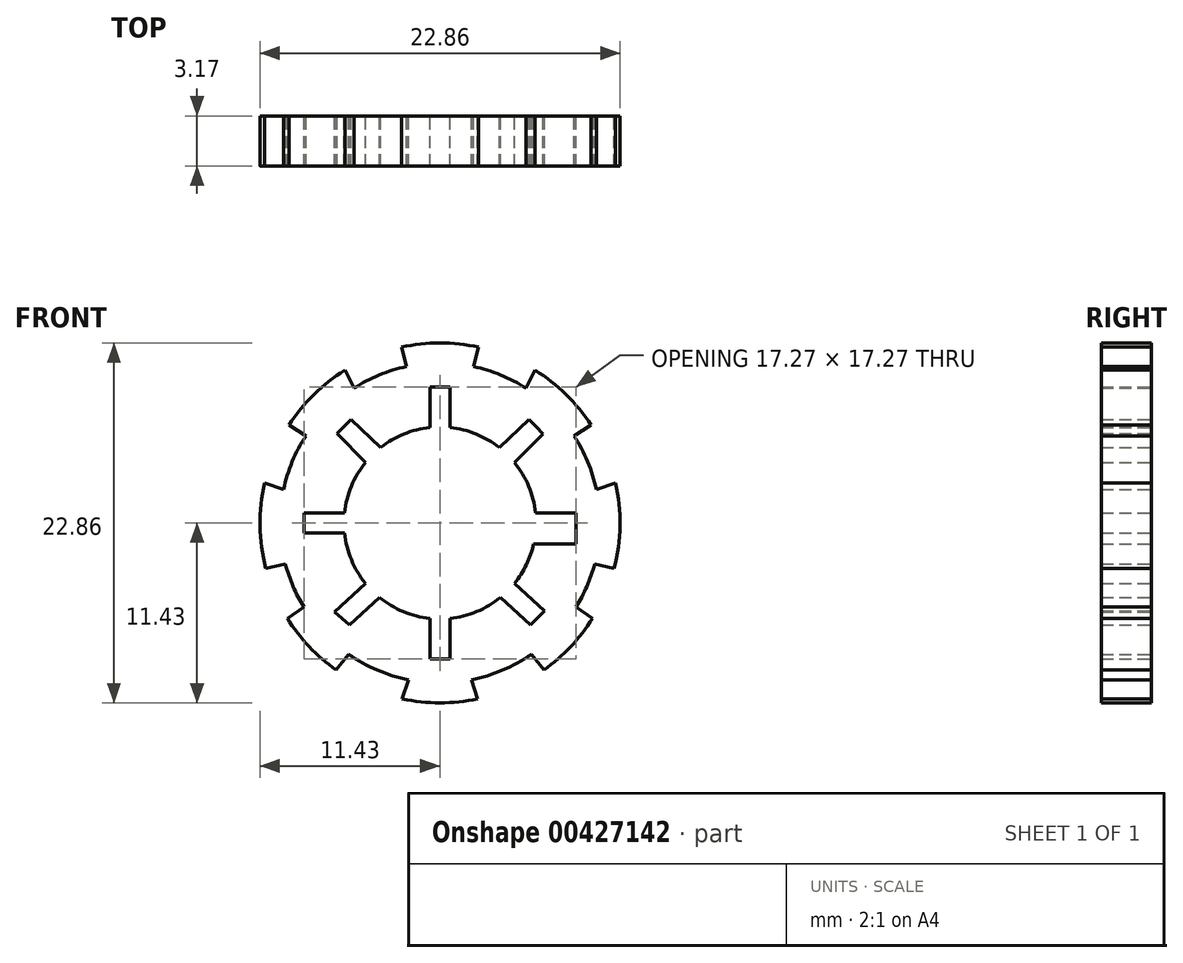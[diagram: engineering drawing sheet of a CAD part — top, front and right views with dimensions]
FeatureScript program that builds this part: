
annotation { "Feature Type Name" : "Feature", "Feature Type Description" : "" }
export const myFeature = defineFeature(function(context is Context, id is Id, definition is map)
    precondition{}
    {
        {
            var Q0;
            Q0=qCreatedBy(makeId("Front.planeOp"),FACE);
            var sketch = newSketch(context, id + "F0", { "sketchPlane" : qUnion([Q0])});
            skCircle(sketch, "E0", {"center": v(0, 0) * mm, "radius": 12.7 * mm});
            skCircle(sketch, "E1", {"center": v(0, 0) * mm, "radius": 11.43 * mm});
            skCircle(sketch, "E2", {"center": v(0, 0) * mm, "radius": 10.16 * mm});
            skCircle(sketch, "E3", {"center": v(0, 0) * mm, "radius": 6.1 * mm});
            skLineSegment(sketch, "E4", {"start": v(0, 8.64) * mm, "end": v(-0.63, 8.64) * mm});
            skLineSegment(sketch, "E5", {"start": v(0, 8.64) * mm, "end": v(0.64, 8.64) * mm});
            skLineSegment(sketch, "E6", {"start": v(6.1, 6.1) * mm, "end": v(5.66, 6.56) * mm});
            skLineSegment(sketch, "E7", {"start": v(6.1, 6.1) * mm, "end": v(6.56, 5.66) * mm});
            skLineSegment(sketch, "E8", {"start": v(8.64, 0) * mm, "end": v(8.64, 0.63) * mm});
            skLineSegment(sketch, "E9", {"start": v(8.64, 0) * mm, "end": v(8.64, -0.64) * mm});
            skLineSegment(sketch, "E10", {"start": v(0, -8.64) * mm, "end": v(-0.63, -8.64) * mm});
            skLineSegment(sketch, "E11", {"start": v(0, -8.64) * mm, "end": v(0.64, -8.64) * mm});
            skLineSegment(sketch, "E12", {"start": v(-8.64, 0) * mm, "end": v(-8.64, 0.63) * mm});
            skLineSegment(sketch, "E13", {"start": v(-8.64, 0) * mm, "end": v(-8.64, -0.64) * mm});
            skLineSegment(sketch, "E14", {"start": v(-6.1, 6.12) * mm, "end": v(-6.54, 5.67) * mm});
            skLineSegment(sketch, "E15", {"start": v(-6.1, 6.12) * mm, "end": v(-5.66, 6.58) * mm});
            skLineSegment(sketch, "E16", {"start": v(-8.64, 0.63) * mm, "end": v(-6.06, 0.63) * mm});
            skLineSegment(sketch, "E17", {"start": v(-8.64, -0.64) * mm, "end": v(-6.06, -0.64) * mm});
            skLineSegment(sketch, "E18", {"start": v(-6.54, 5.67) * mm, "end": v(-4.72, 3.85) * mm});
            skLineSegment(sketch, "E19", {"start": v(-5.66, 6.58) * mm, "end": v(-3.77, 4.8) * mm});
            skLineSegment(sketch, "E20", {"start": v(-0.63, 8.64) * mm, "end": v(-0.63, 6.06) * mm});
            skLineSegment(sketch, "E21", {"start": v(0.64, 8.64) * mm, "end": v(0.64, 6.06) * mm});
            skLineSegment(sketch, "E22", {"start": v(5.66, 6.56) * mm, "end": v(3.84, 4.74) * mm});
            skLineSegment(sketch, "E23", {"start": v(6.56, 5.66) * mm, "end": v(4.74, 3.84) * mm});
            skLineSegment(sketch, "E24", {"start": v(8.64, 0.63) * mm, "end": v(6.06, 0.63) * mm});
            skLineSegment(sketch, "E25", {"start": v(8.64, -0.64) * mm, "end": v(6.06, -0.64) * mm});
            skLineSegment(sketch, "E26", {"start": v(-6.68, -5.64) * mm, "end": v(-4.74, -3.84) * mm});
            skLineSegment(sketch, "E27", {"start": v(-5.73, -6.48) * mm, "end": v(-3.84, -4.73) * mm});
            skLineSegment(sketch, "E28", {"start": v(-0.63, -8.64) * mm, "end": v(-0.63, -6.06) * mm});
            skLineSegment(sketch, "E29", {"start": v(0.64, -8.64) * mm, "end": v(0.64, -6.06) * mm});
            skLineSegment(sketch, "E30", {"start": v(6.63, -5.59) * mm, "end": v(4.74, -3.84) * mm});
            skLineSegment(sketch, "E31", {"start": v(-2.12, 9.94) * mm, "end": v(-2.45, 11.16) * mm});
            skLineSegment(sketch, "E32", {"start": v(-5.47, 8.56) * mm, "end": v(-6.04, 9.7) * mm});
            skLineSegment(sketch, "E33", {"start": v(-8.52, 5.54) * mm, "end": v(-9.6, 6.21) * mm});
            skLineSegment(sketch, "E34", {"start": v(-9.93, 2.13) * mm, "end": v(-11.14, 2.55) * mm});
            skLineSegment(sketch, "E35", {"start": v(-9.82, -2.62) * mm, "end": v(-11.06, -2.88) * mm});
            skLineSegment(sketch, "E36", {"start": v(-8.64, -5.34) * mm, "end": v(-9.7, -6.06) * mm});
            skLineSegment(sketch, "E37", {"start": v(-5.8, -8.34) * mm, "end": v(-6.6, -9.34) * mm});
            skLineSegment(sketch, "E38", {"start": v(-6.68, -5.64) * mm, "end": v(-5.73, -6.48) * mm});
            skLineSegment(sketch, "E39", {"start": v(-6.2, -6.06) * mm, "end": v(-4.31, -4.3) * mm});
            skLineSegment(sketch, "E40", {"start": v(-2, -9.96) * mm, "end": v(-2.4, -11.18) * mm});
            skLineSegment(sketch, "E41.MirrorCS", {"start": v(6.1, 6.12) * mm, "end": v(6.54, 5.67) * mm});
            skLineSegment(sketch, "E42.MirrorCS", {"start": v(6.1, 6.12) * mm, "end": v(5.66, 6.58) * mm});
            skLineSegment(sketch, "E43.MirrorCS", {"start": v(8.64, -5.34) * mm, "end": v(9.7, -6.06) * mm});
            skLineSegment(sketch, "E44.MirrorCS", {"start": v(5.8, -8.34) * mm, "end": v(6.6, -9.34) * mm});
            skLineSegment(sketch, "E45.MirrorCS", {"start": v(2, -9.96) * mm, "end": v(2.4, -11.18) * mm});
            skLineSegment(sketch, "E46.MirrorCS", {"start": v(8.52, 5.54) * mm, "end": v(9.6, 6.21) * mm});
            skLineSegment(sketch, "E47.MirrorCS", {"start": v(2.12, 9.94) * mm, "end": v(2.45, 11.16) * mm});
            skLineSegment(sketch, "E48.MirrorCS", {"start": v(9.82, -2.62) * mm, "end": v(11.06, -2.88) * mm});
            skLineSegment(sketch, "E49.MirrorCS", {"start": v(5.47, 8.56) * mm, "end": v(6.04, 9.7) * mm});
            skLineSegment(sketch, "E50.MirrorCS", {"start": v(9.93, 2.13) * mm, "end": v(11.14, 2.55) * mm});
            skLineSegment(sketch, "E51.MirrorCS", {"start": v(6.54, 5.67) * mm, "end": v(4.72, 3.85) * mm});
            skLineSegment(sketch, "E52.MirrorCS", {"start": v(5.66, 6.58) * mm, "end": v(3.77, 4.8) * mm});
            skLineSegment(sketch, "E53.MirrorCS", {"start": v(5.73, -6.48) * mm, "end": v(3.84, -4.73) * mm});
            skCircle(sketch, "E54", {"center": v(0, 0) * mm, "radius": 4.97 * mm});
            skLineSegment(sketch, "E55", {"start": v(-0.63, -8.64) * mm, "end": v(-1.32, -8.64) * mm});
            skLineSegment(sketch, "E56", {"start": v(0.64, -8.64) * mm, "end": v(1.32, -8.64) * mm});
            skLineSegment(sketch, "E57", {"start": v(-1.32, -8.64) * mm, "end": v(-1.32, -5.95) * mm});
            skLineSegment(sketch, "E58", {"start": v(1.32, -8.64) * mm, "end": v(1.32, -5.95) * mm});
            skLineSegment(sketch, "E59", {"start": v(5.73, -6.48) * mm, "end": v(6.63, -5.59) * mm});
            skLineSegment(sketch, "E60", {"start": v(4.74, -3.84) * mm, "end": v(3.84, -4.73) * mm});
            skLineSegment(sketch, "E61", {"start": v(5.73, -6.48) * mm, "end": v(5.27, -6.98) * mm});
            skLineSegment(sketch, "E62", {"start": v(6.63, -5.59) * mm, "end": v(7.1, -5.08) * mm});
            skLineSegment(sketch, "E63", {"start": v(5.27, -6.98) * mm, "end": v(3.27, -5.14) * mm});
            skLineSegment(sketch, "E64", {"start": v(7.1, -5.08) * mm, "end": v(5.14, -3.28) * mm});
            skLineSegment(sketch, "E65", {"start": v(8.64, -0.64) * mm, "end": v(8.64, -1.32) * mm});
            skLineSegment(sketch, "E66", {"start": v(8.64, 0.63) * mm, "end": v(8.64, 1.32) * mm});
            skLineSegment(sketch, "E67", {"start": v(8.64, 1.32) * mm, "end": v(5.95, 1.32) * mm});
            skLineSegment(sketch, "E68", {"start": v(8.64, -1.32) * mm, "end": v(5.95, -1.32) * mm});
            skSolve(sketch);
        }
        {
            var Q0;
            Q0=makeQuery(id+"F0.imprint","IMPRINT",FACE,{"disambiguationData":[TD([[makeQuery(id+"F0.imprint","IMPRINT",EDGE,{"derivedFrom":sQuery(id+"F0.wireOp",EDGE,"E4")}),-1.0]])]});
            var Q1;
            {var subQ0=sQuery(id+"F0.wireOp",EDGE,"E31");Q1=makeQuery(id+"F0.imprint","IMPRINT",FACE,{"disambiguationData":[TD([[makeQuery(id+"F0.imprint","IMPRINT",EDGE,{"derivedFrom":subQ0}),-1.0]])]});}
            var Q2;
            {var subQ0=sQuery(id+"F0.wireOp",EDGE,"E32");Q2=makeQuery(id+"F0.imprint","IMPRINT",FACE,{"disambiguationData":[TD([[makeQuery(id+"F0.imprint","IMPRINT",EDGE,{"derivedFrom":subQ0}),1.0]])]});}
            var Q3;
            {var subQ0=sQuery(id+"F0.wireOp",EDGE,"E46.MirrorCS");Q3=makeQuery(id+"F0.imprint","IMPRINT",FACE,{"disambiguationData":[TD([[makeQuery(id+"F0.imprint","IMPRINT",EDGE,{"derivedFrom":subQ0}),1.0]])]});}
            var Q4;
            {var subQ0=sQuery(id+"F0.wireOp",EDGE,"E48.MirrorCS");Q4=makeQuery(id+"F0.imprint","IMPRINT",FACE,{"disambiguationData":[TD([[makeQuery(id+"F0.imprint","IMPRINT",EDGE,{"derivedFrom":subQ0}),1.0]])]});}
            var Q5;
            {var subQ0=sQuery(id+"F0.wireOp",EDGE,"E43.MirrorCS");Q5=makeQuery(id+"F0.imprint","IMPRINT",FACE,{"disambiguationData":[TD([[makeQuery(id+"F0.imprint","IMPRINT",EDGE,{"derivedFrom":subQ0}),-1.0]])]});}
            var Q6;
            {var subQ0=sQuery(id+"F0.wireOp",EDGE,"E36");Q6=makeQuery(id+"F0.imprint","IMPRINT",FACE,{"disambiguationData":[TD([[makeQuery(id+"F0.imprint","IMPRINT",EDGE,{"derivedFrom":subQ0}),1.0]])]});}
            var Q7;
            {var subQ0=sQuery(id+"F0.wireOp",EDGE,"E34");Q7=makeQuery(id+"F0.imprint","IMPRINT",FACE,{"disambiguationData":[TD([[makeQuery(id+"F0.imprint","IMPRINT",EDGE,{"derivedFrom":subQ0}),1.0]])]});}
            var Q8;
            Q8=makeQuery(id+"F0.imprint","IMPRINT",FACE,{"disambiguationData":[TD([[makeQuery(id+"F0.imprint","IMPRINT",EDGE,{"derivedFrom":sQuery(id+"F0.wireOp",EDGE,"E0")}),-1.0]])]});
            var Q9;
            {var subQ0=sQuery(id+"F0.wireOp",EDGE,"E40");Q9=makeQuery(id+"F0.imprint","IMPRINT",FACE,{"disambiguationData":[TD([[makeQuery(id+"F0.imprint","IMPRINT",EDGE,{"derivedFrom":subQ0}),1.0]])]});}
            var Q10;
            {var subQ0=sQuery(id+"F0.wireOp",EDGE,"E29");Q10=makeQuery(id+"F0.imprint","IMPRINT",FACE,{"disambiguationData":[TD([[makeQuery(id+"F0.imprint","IMPRINT",EDGE,{"derivedFrom":subQ0}),-1.0]])]});}
            var Q11;
            {var subQ0=sQuery(id+"F0.wireOp",EDGE,"E28");Q11=makeQuery(id+"F0.imprint","IMPRINT",FACE,{"disambiguationData":[TD([[makeQuery(id+"F0.imprint","IMPRINT",EDGE,{"derivedFrom":subQ0}),1.0]])]});}
            var Q12;
            {var subQ0=sQuery(id+"F0.wireOp",EDGE,"E53.MirrorCS");Q12=makeQuery(id+"F0.imprint","IMPRINT",FACE,{"disambiguationData":[TD([[makeQuery(id+"F0.imprint","IMPRINT",EDGE,{"derivedFrom":subQ0}),1.0]])]});}
            var Q13;
            {var subQ0=sQuery(id+"F0.wireOp",EDGE,"E30");Q13=makeQuery(id+"F0.imprint","IMPRINT",FACE,{"disambiguationData":[TD([[makeQuery(id+"F0.imprint","IMPRINT",EDGE,{"derivedFrom":subQ0}),-1.0]])]});}
            var Q14;
            {var subQ0=sQuery(id+"F0.wireOp",EDGE,"E25");Q14=makeQuery(id+"F0.imprint","IMPRINT",FACE,{"disambiguationData":[TD([[makeQuery(id+"F0.imprint","IMPRINT",EDGE,{"derivedFrom":subQ0}),1.0]])]});}
            var Q15;
            {var subQ0=sQuery(id+"F0.wireOp",EDGE,"E24");Q15=makeQuery(id+"F0.imprint","IMPRINT",FACE,{"disambiguationData":[TD([[makeQuery(id+"F0.imprint","IMPRINT",EDGE,{"derivedFrom":subQ0}),-1.0]])]});}
            extrude(context, id + "F1", {"entities" : qUnion([Q0, Q1, Q2, Q3, Q4, Q5, Q6, Q7, Q8, Q9, Q10, Q11, Q12, Q13, Q14, Q15]), "depth" : 3.17 * mm});
        }
    });
